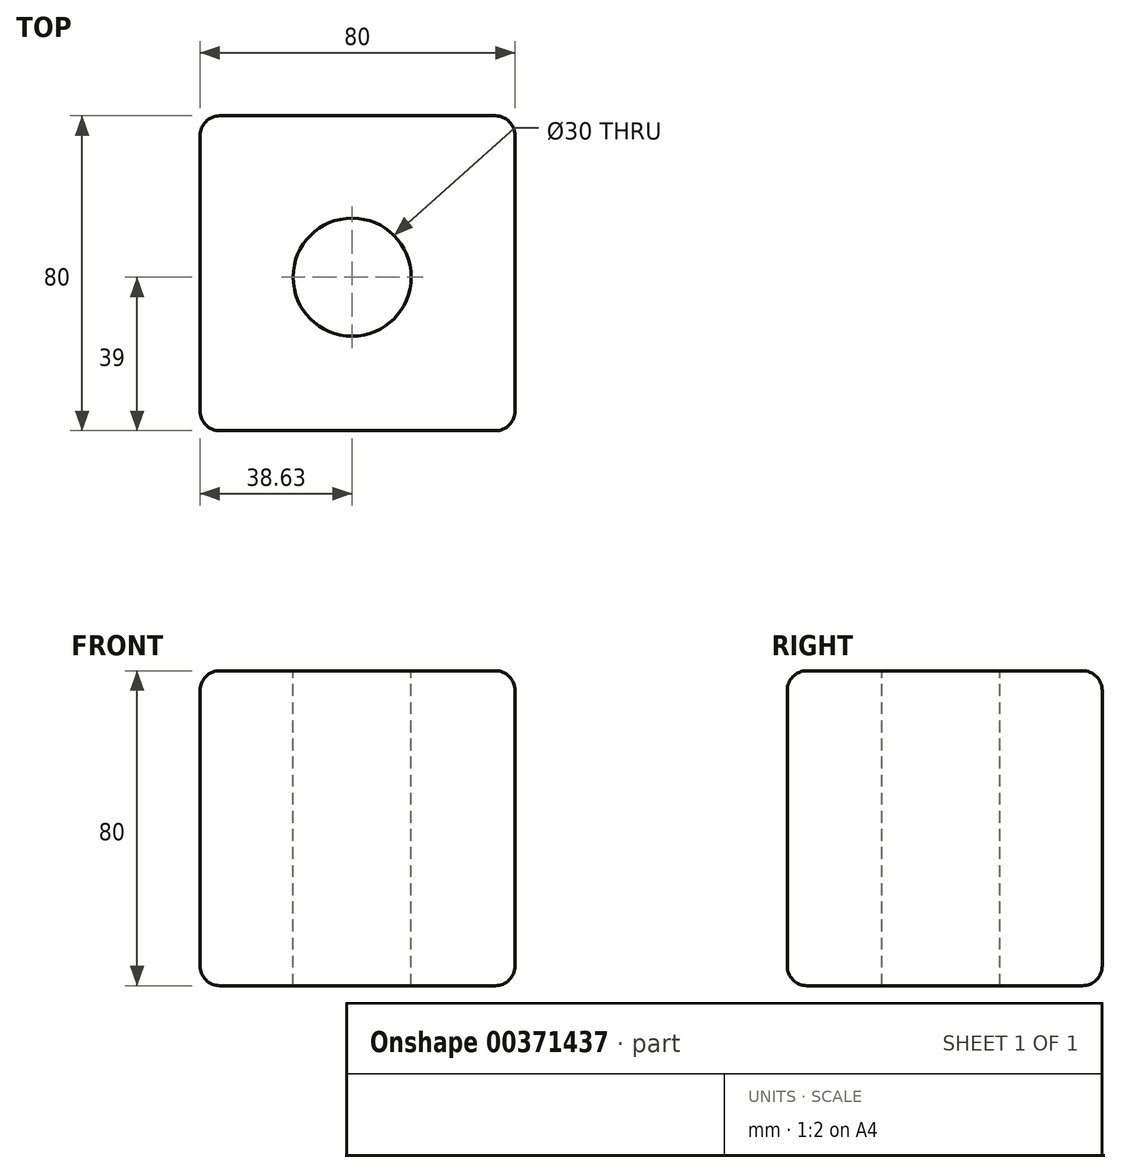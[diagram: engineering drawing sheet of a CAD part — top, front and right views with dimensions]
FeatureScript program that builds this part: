
annotation { "Feature Type Name" : "Feature", "Feature Type Description" : "" }
export const myFeature = defineFeature(function(context is Context, id is Id, definition is map)
    precondition{}
    {
        {
            var Q0;
            Q0=qCreatedBy(makeId("Top.planeOp"),FACE);
            var sketch = newSketch(context, id + "F0", { "sketchPlane" : qUnion([Q0])});
            skLineSegment(sketch, "E0.bottom", {"start": v(-38.63, 57.5) * mm, "end": v(41.37, 57.5) * mm});
            skLineSegment(sketch, "E0.top", {"start": v(-38.63, -22.5) * mm, "end": v(41.37, -22.5) * mm});
            skLineSegment(sketch, "E0.left", {"start": v(-38.63, 57.5) * mm, "end": v(-38.63, -22.5) * mm});
            skLineSegment(sketch, "E0.right", {"start": v(41.37, 57.5) * mm, "end": v(41.37, -22.5) * mm});
            skSolve(sketch);
        }
        {
            var Q0;
            Q0=makeQuery(id+"F0.imprint","IMPRINT",FACE,{"disambiguationData":[TD([[makeQuery(id+"F0.imprint","IMPRINT",EDGE,{"derivedFrom":sQuery(id+"F0.wireOp",EDGE,"E0.bottom")}),-1.0]])]});
            extrude(context, id + "F1", {"entities" : qUnion([Q0]), "depth" : 80 * mm});
        }
        {
            var Q0;
            Q0=makeQuery(id+"F1.opExtrude","CAP_FACE",FACE,{"disambiguationData":[OSD([sQuery(id+"F0.wireOp",EDGE,"E0.bottom"),sQuery(id+"F0.wireOp",EDGE,"E0.top"),sQuery(id+"F0.wireOp",EDGE,"E0.left"),sQuery(id+"F0.wireOp",EDGE,"E0.right")])],"isStart":false});
            var sketch = newSketch(context, id + "F2", { "sketchPlane" : qUnion([Q0])});
            skCircle(sketch, "E1", {"center": v(0, 16.5) * mm, "radius": 15 * mm});
            skSolve(sketch);
        }
        {
            var Q0;
            Q0=makeQuery(id+"F2.imprint","IMPRINT",FACE,{"disambiguationData":[TD([[makeQuery(id+"F2.imprint","IMPRINT",EDGE,{"derivedFrom":sQuery(id+"F2.wireOp",EDGE,"E1")}),1.0]])]});
            extrude(context, id + "F3", {"entities" : qUnion([Q0]), "operationType" : NewBodyOperationType.REMOVE, "endBound" : BoundingType.THROUGH_ALL, "oppositeDirection" : true, "depth" : 25 * mm});
        }
        {
            var Q0;
            Q0=makeQuery(id+"F1.opExtrude","CAP_EDGE",EDGE,{"disambiguationData":[OSD([sQuery(id+"F0.wireOp",EDGE,"E0.bottom")])],"isStart":false});
            var Q1;
            Q1=makeQuery(id+"F1.opExtrude","CAP_EDGE",EDGE,{"disambiguationData":[OSD([sQuery(id+"F0.wireOp",EDGE,"E0.top")])],"isStart":false});
            var Q2;
            Q2=makeQuery(id+"F1.opExtrude","CAP_EDGE",EDGE,{"disambiguationData":[OSD([sQuery(id+"F0.wireOp",EDGE,"E0.left")])],"isStart":false});
            var Q3;
            Q3=makeQuery(id+"F1.opExtrude","CAP_EDGE",EDGE,{"disambiguationData":[OSD([sQuery(id+"F0.wireOp",EDGE,"E0.right")])],"isStart":false});
            var Q4;
            Q4=makeQuery(id+"F1.opExtrude","SWEPT_EDGE",EDGE,{"disambiguationData":[OSD([sQuery(id+"F0.wireOp",EDGE,"E0.bottom"),sQuery(id+"F0.wireOp",EDGE,"E0.right")])]});
            var Q5;
            Q5=makeQuery(id+"F1.opExtrude","SWEPT_EDGE",EDGE,{"disambiguationData":[OSD([sQuery(id+"F0.wireOp",EDGE,"E0.top"),sQuery(id+"F0.wireOp",EDGE,"E0.right")])]});
            var Q6;
            Q6=makeQuery(id+"F1.opExtrude","CAP_EDGE",EDGE,{"disambiguationData":[OSD([sQuery(id+"F0.wireOp",EDGE,"E0.right")])],"isStart":true});
            var Q7;
            Q7=makeQuery(id+"F1.opExtrude","SWEPT_EDGE",EDGE,{"disambiguationData":[OSD([sQuery(id+"F0.wireOp",EDGE,"E0.bottom"),sQuery(id+"F0.wireOp",EDGE,"E0.left")])]});
            var Q8;
            Q8=makeQuery(id+"F1.opExtrude","CAP_EDGE",EDGE,{"disambiguationData":[OSD([sQuery(id+"F0.wireOp",EDGE,"E0.left")])],"isStart":true});
            var Q9;
            Q9=makeQuery(id+"F1.opExtrude","SWEPT_EDGE",EDGE,{"disambiguationData":[OSD([sQuery(id+"F0.wireOp",EDGE,"E0.top"),sQuery(id+"F0.wireOp",EDGE,"E0.left")])]});
            var Q10;
            Q10=makeQuery(id+"F1.opExtrude","SWEPT_FACE",FACE,{"disambiguationData":[OSD([sQuery(id+"F0.wireOp",EDGE,"E0.bottom")])]});
            var Q11;
            Q11=makeQuery(id+"F1.opExtrude","CAP_EDGE",EDGE,{"disambiguationData":[OSD([sQuery(id+"F0.wireOp",EDGE,"E0.top")])],"isStart":true});
            fillet(context, id + "F4", {"entities" : qUnion([Q0, Q1, Q2, Q3, Q4, Q5, Q6, Q7, Q8, Q9, Q10, Q11]), "radius" : 5 * mm, "tangentPropagation" : true, "allowEdgeOverflow" : false});
        }
    });
